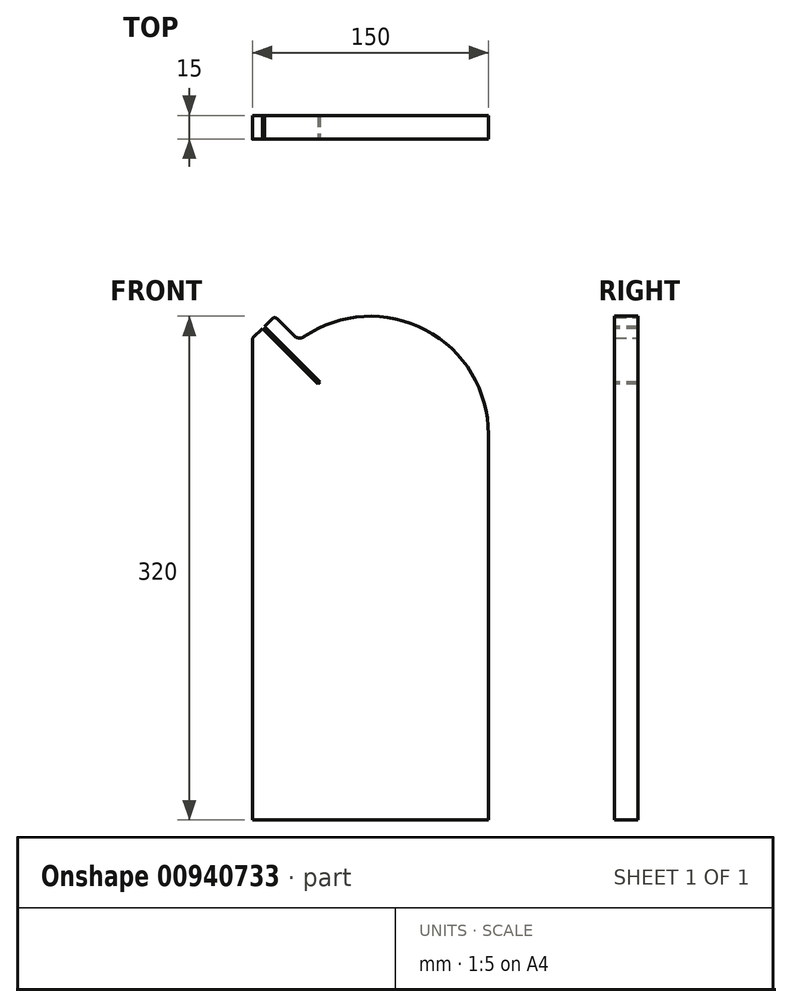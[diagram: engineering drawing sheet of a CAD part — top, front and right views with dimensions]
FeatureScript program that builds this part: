
annotation { "Feature Type Name" : "Feature", "Feature Type Description" : "" }
export const myFeature = defineFeature(function(context is Context, id is Id, definition is map)
    precondition{}
    {
        {
            var Q0;
            Q0=qCreatedBy(makeId("Front.planeOp"),FACE);
            var sketch = newSketch(context, id + "F0", { "sketchPlane" : qUnion([Q0])});
            skLineSegment(sketch, "E0.bottom", {"start": v(-75, 0) * mm, "end": v(75, 0) * mm});
            skLineSegment(sketch, "E0.left", {"start": v(-75, 0) * mm, "end": v(-75, 305.76) * mm});
            skLineSegment(sketch, "E0.right", {"start": v(75, 0) * mm, "end": v(75, 245) * mm});
            skArc(sketch, "E1", {"start": v(75, 245) * mm, "mid": v(33.24, 312.23) * mm, "end": v(-45.54, 304.6) * mm});
            skLineSegment(sketch, "E2", {"start": v(-75, 305.76) * mm, "end": v(-60.86, 319.9) * mm});
            skLineSegment(sketch, "E3", {"start": v(-60.86, 319.9) * mm, "end": v(-45.54, 304.6) * mm});
            skSolve(sketch);
        }
        {
            var Q0;
            Q0 = qSketchRegion(id + "F0", true);
            extrude(context, id + "F1", {"entities" : qUnion([Q0]), "depth" : 15 * mm, "offsetDistance" : 25 * mm});
        }
        {
            var Q0;
            Q0=makeQuery(id+"F1.opExtrude","SWEPT_EDGE",EDGE,{"disambiguationData":[OSD([sQuery(id+"F0.wireOp",EDGE,"E1"),sQuery(id+"F0.wireOp",EDGE,"E3")])]});
            fillet(context, id + "F2", {"entities" : qUnion([Q0]), "radius" : 5 * mm, "tangentPropagation" : true, "allowEdgeOverflow" : false});
        }
        {
            var Q0;
            Q0=makeQuery(id+"F1.opExtrude","SWEPT_EDGE",EDGE,{"disambiguationData":[OSD([sQuery(id+"F0.wireOp",EDGE,"E2"),sQuery(id+"F0.wireOp",EDGE,"E3")])]});
            fillet(context, id + "F3", {"entities" : qUnion([Q0]), "radius" : 2 * mm, "tangentPropagation" : true, "allowEdgeOverflow" : false});
        }
        {
            var Q0;
            Q0=makeQuery(id+"F1.opExtrude","SWEPT_EDGE",EDGE,{"disambiguationData":[OSD([sQuery(id+"F0.wireOp",EDGE,"E0.left"),sQuery(id+"F0.wireOp",EDGE,"E2")])]});
            fillet(context, id + "F4", {"entities" : qUnion([Q0]), "radius" : 2 * mm, "tangentPropagation" : true, "allowEdgeOverflow" : false});
        }
        {
            var Q0;
            Q0=makeQuery(id+"F1.opExtrude","CAP_FACE",FACE,{"disambiguationData":[OSD([sQuery(id+"F0.wireOp",EDGE,"E0.bottom"),sQuery(id+"F0.wireOp",EDGE,"E0.left"),sQuery(id+"F0.wireOp",EDGE,"E0.right"),sQuery(id+"F0.wireOp",EDGE,"E1"),sQuery(id+"F0.wireOp",EDGE,"E2"),sQuery(id+"F0.wireOp",EDGE,"E3")])],"isStart":false});
            var sketch = newSketch(context, id + "F5", { "sketchPlane" : qUnion([Q0])});
            skLineSegment(sketch, "E4", {"start": v(-68.64, 312.13) * mm, "end": v(-33.3, 276.8) * mm});
            skLineSegment(sketch, "E5", {"start": v(-33.3, 276.8) * mm, "end": v(-31.9, 278.22) * mm});
            skLineSegment(sketch, "E6", {"start": v(-31.9, 278.22) * mm, "end": v(-67.22, 313.54) * mm});
            skLineSegment(sketch, "E7", {"start": v(-67.22, 313.54) * mm, "end": v(-68.64, 312.13) * mm});
            skSolve(sketch);
        }
        {
            var Q0;
            Q0 = qSketchRegion(id + "F5", true);
            extrude(context, id + "F6", {"entities" : qUnion([Q0]), "operationType" : NewBodyOperationType.REMOVE, "endBound" : BoundingType.THROUGH_ALL, "oppositeDirection" : true, "depth" : 25 * mm, "offsetDistance" : 25 * mm});
        }
        {
            var Q0;
            Q0=makeQuery(id+"F1.opExtrude","SWEPT_FACE",FACE,{"disambiguationData":[OSD([sQuery(id+"F0.wireOp",EDGE,"E3")])]});
            var sketch = newSketch(context, id + "F7", { "sketchPlane" : qUnion([Q0])});
            skCircle(sketch, "E8", {"center": v(-259.24, -7.5) * mm, "radius": 3.1 * mm});
            skSolve(sketch);
        }
        {
            var Q0;
            Q0 = qSketchRegion(id + "F7", true);
            var Q1;
            Q1=makeQuery(id+"F6.boolean.opBoolean","COPY",FACE,{"derivedFrom":makeQuery(id+"F6.opExtrude","SWEPT_FACE",FACE,{"disambiguationData":[OSD([sQuery(id+"F5.wireOp",EDGE,"E6")])]})});
            extrude(context, id + "F8", {"entities" : qUnion([Q0]), "operationType" : NewBodyOperationType.REMOVE, "endBound" : BoundingType.UP_TO_SURFACE, "oppositeDirection" : true, "depth" : 25 * mm, "endBoundEntityFace" : qUnion([Q1]), "offsetDistance" : 25 * mm});
        }
    });
